# Revit family: London
name_source: partatom
category: Lighting Fixtures
revit_build: Autodesk Revit MEP 2012 (Build: 20110916_2132(x64)
units: mm (PartAtom-declared; Revit-internal decimal feet)

## types (12) — shared parameters
Apparent Load = 0 VA
Black Matte Textured = 0.00"
Default Elevation = 48.00"
Description = Village Collection
Glass = Hubbell - Glass
Lamp = LED Array
Manufacturer = Beacon Lighting
Manufacturer Fax = 941-751-5535
Model = London
Product Documentation Link = http://www.beaconproducts.com
Product Page URL = http://www.beaconproducts.com
Total Input Wattage = 55,80 & 110 Watts
URL = http://www.beaconproducts.com
Voltage = 120 V

## per-type parameters (varying)
| type | Product Material |
| Basic Black Textured | Paint - Hubbell - Basic Black Textured |
| Black Matte Textured | Paint - Hubbell - Black Matte Textured |
| Bronze Textured | Paint - Hubbell - Bronze Textured |
| Dark Bronze Textured | Paint - Hubbell - Dark Bronze Textured |
| Dark Platinum Smooth | Paint - Hubbell - Dark Platinum Smooth |
| Gray Smooth | Paint - Hubbell - Gray Smooth |
| Green Textured | Paint - Hubbell - Green Textured |
| Metallic Bronze Textured | Paint - Hubbell - Metallic Bronze Textured |
| Metallic Silver Textured | Paint - Hubbell - Metallic Silver Textured |
| Metallic Titanium Textured | Paint - Hubbell - Metallic Titanium Textured |
| Old World Iron | Paint - Hubbell - Old World Iron |
| White Texture | Paint - Hubbell - White Texture |

## geometry (parser evidence)
native form markers: Sweep x4
no freeform markers — native parametric forms only
